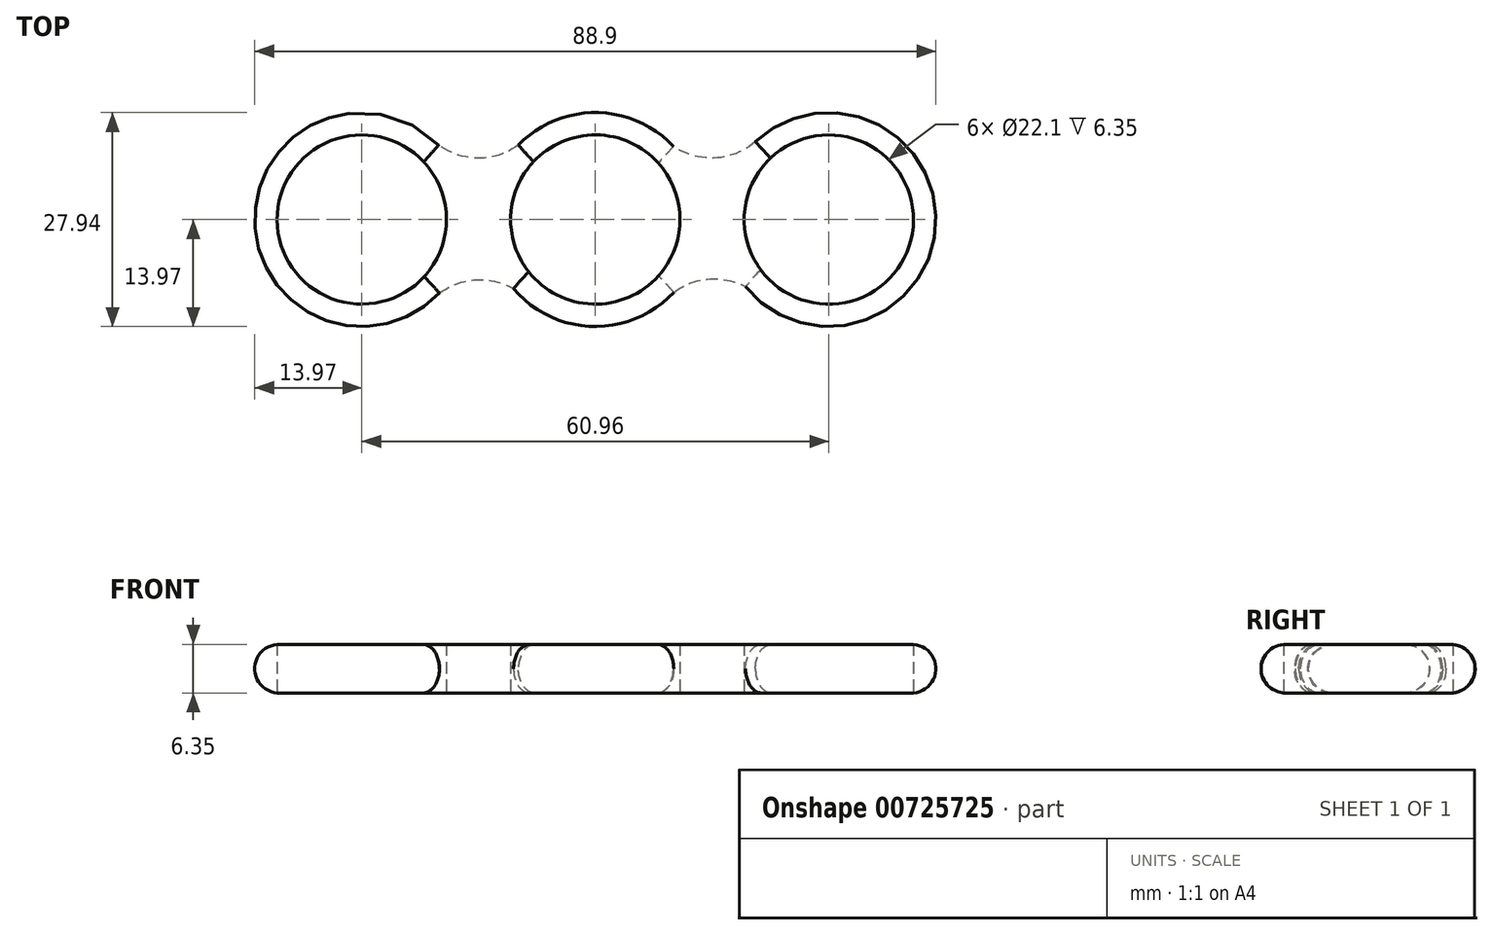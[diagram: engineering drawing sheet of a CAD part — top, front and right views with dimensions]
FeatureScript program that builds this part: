
annotation { "Feature Type Name" : "Feature", "Feature Type Description" : "" }
export const myFeature = defineFeature(function(context is Context, id is Id, definition is map)
    precondition{}
    {
        {
            var Q0;
            Q0=qCreatedBy(makeId("Top.planeOp"),FACE);
            var sketch = newSketch(context, id + "F0", { "sketchPlane" : qUnion([Q0])});
            skCircle(sketch, "E0", {"center": v(0, 0) * mm, "radius": 11.05 * mm});
            skCircle(sketch, "E1", {"center": v(0, 0) * mm, "radius": 13.97 * mm});
            skLineSegment(sketch, "E2", {"start": v(0, 0) * mm, "end": v(-30.48, 0) * mm});
            skCircle(sketch, "E3", {"center": v(-30.48, 0) * mm, "radius": 11.05 * mm});
            skCircle(sketch, "E4", {"center": v(-30.48, 0) * mm, "radius": 13.97 * mm});
            skLineSegment(sketch, "E5", {"start": v(0, 0) * mm, "end": v(30.48, 0) * mm});
            skCircle(sketch, "E6", {"center": v(30.48, 0) * mm, "radius": 11.05 * mm});
            skCircle(sketch, "E7", {"center": v(30.48, 0) * mm, "radius": 13.97 * mm});
            skArc(sketch, "E8", {"start": v(-7.96, -11.48) * mm, "mid": v(-14.64, -7.85) * mm, "end": v(-21.65, -10.83) * mm});
            skArc(sketch, "E9.0.1.0", {"start": v(-21.76, 10.91) * mm, "mid": v(-15.24, 8) * mm, "end": v(-8.72, 10.91) * mm});
            skArc(sketch, "E9.1.0.0", {"start": v(22.79, -11.66) * mm, "mid": v(16.02, -7.77) * mm, "end": v(8.83, -10.82) * mm});
            skLineSegment(sketch, "E9.direction1", {"start": v(-15.06, -16.6) * mm, "end": v(15.5, -16.51) * mm, "construction": true});
            skLineSegment(sketch, "E9.direction2", {"start": v(-15.06, -16.6) * mm, "end": v(-15.24, 16.76) * mm, "construction": true});
            skLineSegment(sketch, "E10.direction1", {"start": v(15.5, -16.5) * mm, "end": v(15.24, 17.02) * mm, "construction": true});
            skArc(sketch, "E11.1.0.0", {"start": v(8.64, 10.92) * mm, "mid": v(15.15, 8.02) * mm, "end": v(21.67, 10.92) * mm});
            skLineSegment(sketch, "E11.direction1", {"start": v(-21.76, 10.91) * mm, "end": v(8.64, 10.92) * mm, "construction": true});
            skPoint(sketch, "E12.orphan", {"position": v(39.03, 10.93) * mm});
            skSolve(sketch);
        }
        {
            var Q0;
            Q0 = qSketchRegion(id + "F0", true);
            extrude(context, id + "F1", {"entities" : qUnion([Q0]), "depth" : 6.35 * mm, "offsetDistance" : 25.4 * mm});
        }
        {
            var Q0;
            Q0=makeQuery(id+"F1.opExtrude","CAP_EDGE",EDGE,{"disambiguationData":[OSD([sQuery(id+"F0.wireOp",EDGE,"E4")])],"isStart":false});
            var Q1;
            {var subQ0=sQuery(id+"F0.wireOp",EDGE,"E9.0.1.0");var subQ1=sQuery(id+"F0.wireOp",EDGE,"E1");var subQ2=makeQuery(id+"F0.imprint","INTERSECT",VERTEX,{"disambiguationData":[OD(0.0)],"derivedFrom":[subQ1,subQ0]});Q1=makeQuery(id+"F1.opExtrude","CAP_EDGE",EDGE,{"disambiguationData":[OSD([subQ1]),TDD([makeQuery(id+"F0.imprint","IMPRINT",EDGE,{"disambiguationData":[TD([[subQ2,1.0]])],"derivedFrom":subQ1}),makeQuery(id+"F0.imprint","IMPRINT",EDGE,{"disambiguationData":[TD([[subQ2,-1.0]])],"derivedFrom":subQ1})])],"isStart":false});}
            var Q2;
            Q2=makeQuery(id+"F1.opExtrude","CAP_EDGE",EDGE,{"disambiguationData":[OSD([sQuery(id+"F0.wireOp",EDGE,"E9.0.1.0")])],"isStart":false});
            var Q3;
            Q3=makeQuery(id+"F1.opExtrude","CAP_EDGE",EDGE,{"disambiguationData":[OSD([sQuery(id+"F0.wireOp",EDGE,"E11.1.0.0")])],"isStart":false});
            var Q4;
            Q4=makeQuery(id+"F1.opExtrude","CAP_EDGE",EDGE,{"disambiguationData":[OSD([sQuery(id+"F0.wireOp",EDGE,"E7")])],"isStart":false});
            var Q5;
            {var subQ0=sQuery(id+"F0.wireOp",EDGE,"E9.1.0.0");var subQ1=sQuery(id+"F0.wireOp",EDGE,"E1");var subQ2=makeQuery(id+"F0.imprint","INTERSECT",VERTEX,{"disambiguationData":[OD(0.0)],"derivedFrom":[subQ1,subQ0]});var subQ3=sQuery(id+"F0.wireOp",EDGE,"E8");var subQ4=makeQuery(id+"F0.imprint","INTERSECT",VERTEX,{"disambiguationData":[OD(0.0)],"derivedFrom":[subQ1,subQ3]});Q5=makeQuery(id+"F1.opExtrude","CAP_EDGE",EDGE,{"disambiguationData":[OSD([subQ1]),TDD([makeQuery(id+"F0.imprint","IMPRINT",EDGE,{"disambiguationData":[TD([[subQ4,1.0]])],"derivedFrom":subQ1}),makeQuery(id+"F0.imprint","IMPRINT",EDGE,{"disambiguationData":[TD([[subQ4,-1.0]])],"derivedFrom":subQ1}),makeQuery(id+"F0.imprint","IMPRINT",EDGE,{"disambiguationData":[TD([[subQ2,-1.0]])],"derivedFrom":subQ1})])],"isStart":false});}
            var Q6;
            Q6=makeQuery(id+"F1.opExtrude","CAP_EDGE",EDGE,{"disambiguationData":[OSD([sQuery(id+"F0.wireOp",EDGE,"E9.1.0.0")])],"isStart":false});
            var Q7;
            Q7=makeQuery(id+"F1.opExtrude","CAP_EDGE",EDGE,{"disambiguationData":[OSD([sQuery(id+"F0.wireOp",EDGE,"E8")])],"isStart":false});
            var Q8;
            Q8=makeQuery(id+"F1.opExtrude","CAP_EDGE",EDGE,{"disambiguationData":[OSD([sQuery(id+"F0.wireOp",EDGE,"E9.0.1.0")])],"isStart":true});
            var Q9;
            Q9=makeQuery(id+"F1.opExtrude","CAP_EDGE",EDGE,{"disambiguationData":[OSD([sQuery(id+"F0.wireOp",EDGE,"E8")])],"isStart":true});
            var Q10;
            Q10=makeQuery(id+"F1.opExtrude","CAP_EDGE",EDGE,{"disambiguationData":[OSD([sQuery(id+"F0.wireOp",EDGE,"E4")])],"isStart":true});
            var Q11;
            {var subQ0=sQuery(id+"F0.wireOp",EDGE,"E9.1.0.0");var subQ1=sQuery(id+"F0.wireOp",EDGE,"E1");var subQ2=makeQuery(id+"F0.imprint","INTERSECT",VERTEX,{"disambiguationData":[OD(0.0)],"derivedFrom":[subQ1,subQ0]});var subQ3=sQuery(id+"F0.wireOp",EDGE,"E8");var subQ4=makeQuery(id+"F0.imprint","INTERSECT",VERTEX,{"disambiguationData":[OD(0.0)],"derivedFrom":[subQ1,subQ3]});Q11=makeQuery(id+"F1.opExtrude","CAP_EDGE",EDGE,{"disambiguationData":[OSD([subQ1]),TDD([makeQuery(id+"F0.imprint","IMPRINT",EDGE,{"disambiguationData":[TD([[subQ4,1.0]])],"derivedFrom":subQ1}),makeQuery(id+"F0.imprint","IMPRINT",EDGE,{"disambiguationData":[TD([[subQ4,-1.0]])],"derivedFrom":subQ1}),makeQuery(id+"F0.imprint","IMPRINT",EDGE,{"disambiguationData":[TD([[subQ2,-1.0]])],"derivedFrom":subQ1})])],"isStart":true});}
            var Q12;
            {var subQ0=sQuery(id+"F0.wireOp",EDGE,"E9.0.1.0");var subQ1=sQuery(id+"F0.wireOp",EDGE,"E1");var subQ2=makeQuery(id+"F0.imprint","INTERSECT",VERTEX,{"disambiguationData":[OD(0.0)],"derivedFrom":[subQ1,subQ0]});Q12=makeQuery(id+"F1.opExtrude","CAP_EDGE",EDGE,{"disambiguationData":[OSD([subQ1]),TDD([makeQuery(id+"F0.imprint","IMPRINT",EDGE,{"disambiguationData":[TD([[subQ2,1.0]])],"derivedFrom":subQ1}),makeQuery(id+"F0.imprint","IMPRINT",EDGE,{"disambiguationData":[TD([[subQ2,-1.0]])],"derivedFrom":subQ1})])],"isStart":true});}
            var Q13;
            Q13=makeQuery(id+"F1.opExtrude","CAP_EDGE",EDGE,{"disambiguationData":[OSD([sQuery(id+"F0.wireOp",EDGE,"E7")])],"isStart":true});
            var Q14;
            Q14=makeQuery(id+"F1.opExtrude","CAP_EDGE",EDGE,{"disambiguationData":[OSD([sQuery(id+"F0.wireOp",EDGE,"E9.1.0.0")])],"isStart":true});
            var Q15;
            Q15=makeQuery(id+"F1.opExtrude","CAP_EDGE",EDGE,{"disambiguationData":[OSD([sQuery(id+"F0.wireOp",EDGE,"E11.1.0.0")])],"isStart":true});
            fillet(context, id + "F2", {"entities" : qUnion([Q0, Q1, Q2, Q3, Q4, Q5, Q6, Q7, Q8, Q9, Q10, Q11, Q12, Q13, Q14, Q15]), "radius" : 3.17 * mm, "tangentPropagation" : true, "allowEdgeOverflow" : false});
        }
    });
